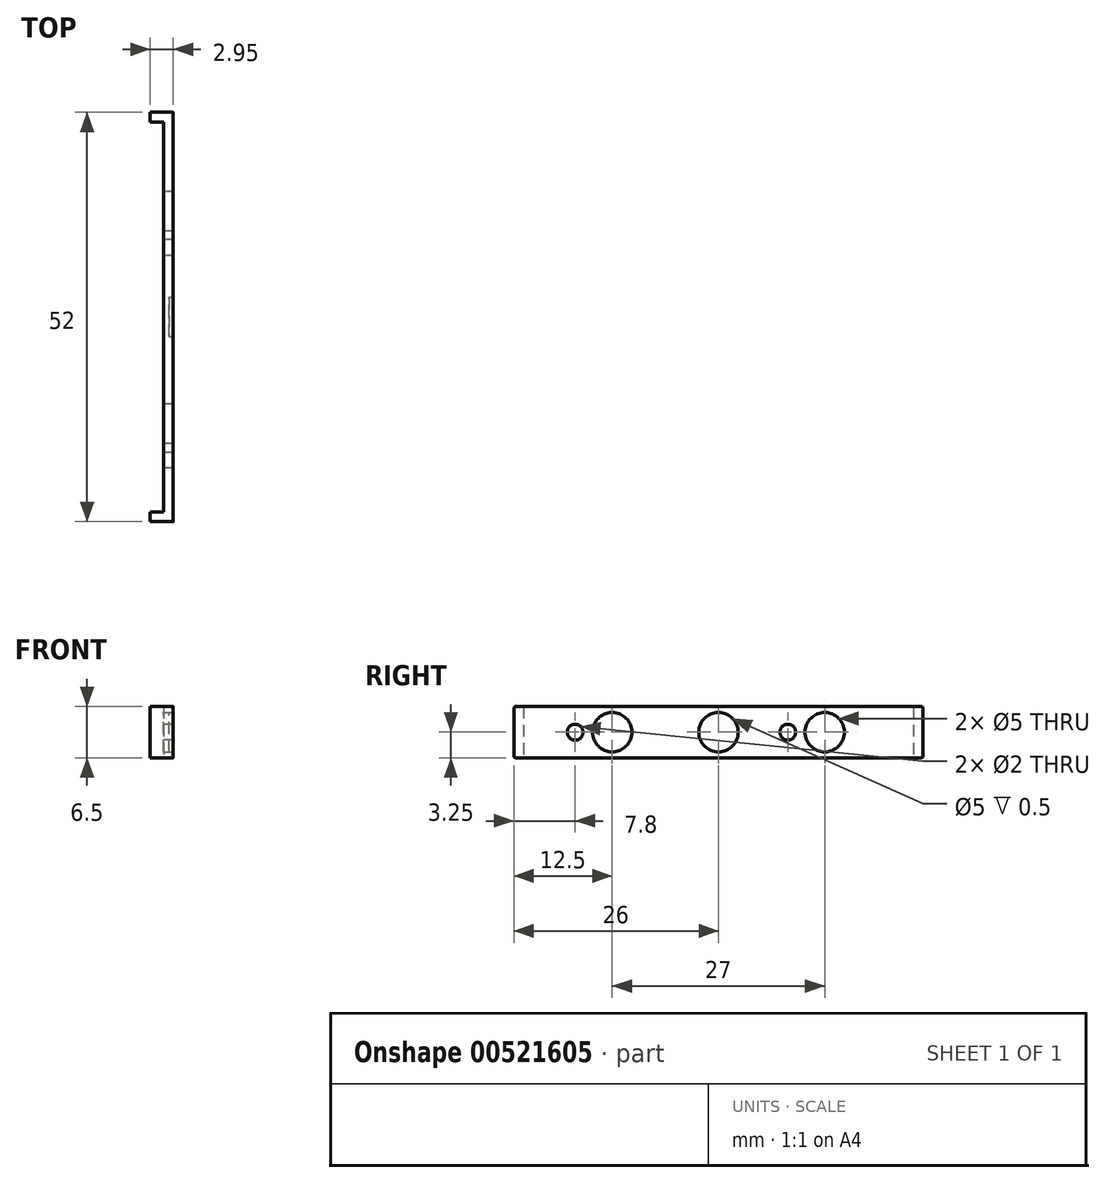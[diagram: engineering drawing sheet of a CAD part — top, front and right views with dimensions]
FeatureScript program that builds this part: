
annotation { "Feature Type Name" : "Feature", "Feature Type Description" : "" }
export const myFeature = defineFeature(function(context is Context, id is Id, definition is map)
    precondition{}
    {
        {
            var Q0;
            Q0=qCreatedBy(makeId("Right.planeOp"),FACE);
            var sketch = newSketch(context, id + "F0", { "sketchPlane" : qUnion([Q0])});
            skLineSegment(sketch, "E0.bottom", {"start": v(26, 3.25) * mm, "end": v(-26, 3.25) * mm});
            skLineSegment(sketch, "E0.top", {"start": v(26, -3.25) * mm, "end": v(-26, -3.25) * mm});
            skLineSegment(sketch, "E0.left", {"start": v(26, 3.25) * mm, "end": v(26, -3.25) * mm});
            skLineSegment(sketch, "E0.right", {"start": v(-26, 3.25) * mm, "end": v(-26, -3.25) * mm});
            skPoint(sketch, "E0.middle", {"position": v(0, 0) * mm});
            skSolve(sketch);
        }
        {
            var Q0;
            Q0=makeQuery(id+"F0.imprint","IMPRINT",FACE,{"disambiguationData":[TD([[makeQuery(id+"F0.imprint","IMPRINT",EDGE,{"derivedFrom":sQuery(id+"F0.wireOp",EDGE,"E0.bottom")}),1.0]])]});
            extrude(context, id + "F1", {"entities" : qUnion([Q0]), "endBound" : BoundingType.SYMMETRIC, "depth" : 1.25 * mm, "offsetDistance" : 25 * mm});
        }
        {
            var Q0;
            Q0=makeQuery(id+"F1.opExtrude","CAP_FACE",FACE,{"disambiguationData":[OSD([sQuery(id+"F0.wireOp",EDGE,"E0.bottom"),sQuery(id+"F0.wireOp",EDGE,"E0.top"),sQuery(id+"F0.wireOp",EDGE,"E0.left"),sQuery(id+"F0.wireOp",EDGE,"E0.right")])],"isStart":true});
            var sketch = newSketch(context, id + "F2", { "sketchPlane" : qUnion([Q0])});
            skLineSegment(sketch, "E1.bottom", {"start": v(-26, 3.25) * mm, "end": v(-24.75, 3.25) * mm});
            skLineSegment(sketch, "E1.top", {"start": v(-26, -3.25) * mm, "end": v(-24.75, -3.25) * mm});
            skLineSegment(sketch, "E1.left", {"start": v(-26, 3.25) * mm, "end": v(-26, -3.25) * mm});
            skLineSegment(sketch, "E1.right", {"start": v(-24.75, 3.25) * mm, "end": v(-24.75, -3.25) * mm});
            skLineSegment(sketch, "E2.bottom", {"start": v(24.75, 3.25) * mm, "end": v(26, 3.25) * mm});
            skLineSegment(sketch, "E2.top", {"start": v(24.75, -3.25) * mm, "end": v(26, -3.25) * mm});
            skLineSegment(sketch, "E2.left", {"start": v(24.75, 3.25) * mm, "end": v(24.75, -3.25) * mm});
            skLineSegment(sketch, "E2.right", {"start": v(26, 3.25) * mm, "end": v(26, -3.25) * mm});
            skSolve(sketch);
        }
        {
            var Q0;
            Q0 = qSketchRegion(id + "F2", true);
            extrude(context, id + "F3", {"entities" : qUnion([Q0]), "operationType" : NewBodyOperationType.ADD, "depth" : 1.7 * mm, "offsetDistance" : 25 * mm});
        }
        {
            var Q0;
            Q0=makeQuery(id+"F3.boolean.opBoolean","MERGE",EDGE,{"derivedFrom":[makeQuery(id+"F1.opExtrude","SWEPT_EDGE",EDGE,{"disambiguationData":[OSD([sQuery(id+"F0.wireOp",EDGE,"E0.bottom"),sQuery(id+"F0.wireOp",EDGE,"E0.right")])]}),makeQuery(id+"F3.opExtrude","SWEPT_EDGE",EDGE,{"disambiguationData":[OSD([sQuery(id+"F2.wireOp",EDGE,"E2.bottom"),sQuery(id+"F2.wireOp",EDGE,"E2.right")])]})]});
            var Q1;
            Q1=makeQuery(id+"F3.boolean.opBoolean","MERGE",EDGE,{"derivedFrom":[makeQuery(id+"F1.opExtrude","SWEPT_EDGE",EDGE,{"disambiguationData":[OSD([sQuery(id+"F0.wireOp",EDGE,"E0.top"),sQuery(id+"F0.wireOp",EDGE,"E0.right")])]}),makeQuery(id+"F3.opExtrude","SWEPT_EDGE",EDGE,{"disambiguationData":[OSD([sQuery(id+"F2.wireOp",EDGE,"E2.top"),sQuery(id+"F2.wireOp",EDGE,"E2.right")])]})]});
            var Q2;
            Q2=makeQuery(id+"F3.boolean.opBoolean","MERGE",EDGE,{"derivedFrom":[makeQuery(id+"F1.opExtrude","SWEPT_EDGE",EDGE,{"disambiguationData":[OSD([sQuery(id+"F0.wireOp",EDGE,"E0.bottom"),sQuery(id+"F0.wireOp",EDGE,"E0.left")])]}),makeQuery(id+"F3.opExtrude","SWEPT_EDGE",EDGE,{"disambiguationData":[OSD([sQuery(id+"F2.wireOp",EDGE,"E1.bottom"),sQuery(id+"F2.wireOp",EDGE,"E1.left")])]})]});
            var Q3;
            Q3=makeQuery(id+"F3.boolean.opBoolean","MERGE",EDGE,{"derivedFrom":[makeQuery(id+"F1.opExtrude","SWEPT_EDGE",EDGE,{"disambiguationData":[OSD([sQuery(id+"F0.wireOp",EDGE,"E0.top"),sQuery(id+"F0.wireOp",EDGE,"E0.left")])]}),makeQuery(id+"F3.opExtrude","SWEPT_EDGE",EDGE,{"disambiguationData":[OSD([sQuery(id+"F2.wireOp",EDGE,"E1.top"),sQuery(id+"F2.wireOp",EDGE,"E1.left")])]})]});
            fillet(context, id + "F4", {"entities" : qUnion([Q0, Q1, Q2, Q3]), "radius" : .25 * mm, "tangentPropagation" : true, "allowEdgeOverflow" : false});
        }
        {
            var Q0;
            Q0=makeQuery(id+"F1.opExtrude","CAP_FACE",FACE,{"disambiguationData":[OSD([sQuery(id+"F0.wireOp",EDGE,"E0.bottom"),sQuery(id+"F0.wireOp",EDGE,"E0.top"),sQuery(id+"F0.wireOp",EDGE,"E0.left"),sQuery(id+"F0.wireOp",EDGE,"E0.right")])],"isStart":false});
            var sketch = newSketch(context, id + "F5", { "sketchPlane" : qUnion([Q0])});
            skCircle(sketch, "E3", {"center": v(-13.5, 0) * mm, "radius": 2.5 * mm});
            skCircle(sketch, "E4", {"center": v(13.5, 0) * mm, "radius": 2.5 * mm});
            skSolve(sketch);
        }
        {
            var Q0;
            Q0 = qSketchRegion(id + "F5", true);
            extrude(context, id + "F6", {"entities" : qUnion([Q0]), "operationType" : NewBodyOperationType.REMOVE, "endBound" : BoundingType.UP_TO_NEXT, "oppositeDirection" : true, "depth" : 25 * mm, "offsetDistance" : 25 * mm});
        }
        {
            var Q0;
            Q0=makeQuery(id+"F1.opExtrude","CAP_FACE",FACE,{"disambiguationData":[OSD([sQuery(id+"F0.wireOp",EDGE,"E0.bottom"),sQuery(id+"F0.wireOp",EDGE,"E0.top"),sQuery(id+"F0.wireOp",EDGE,"E0.left"),sQuery(id+"F0.wireOp",EDGE,"E0.right")])],"isStart":true});
            var sketch = newSketch(context, id + "F7", { "sketchPlane" : qUnion([Q0])});
            skCircle(sketch, "E5", {"center": v(-8.8, 0) * mm, "radius": 1 * mm});
            skCircle(sketch, "E6", {"center": v(18.2, 0) * mm, "radius": 1 * mm});
            skSolve(sketch);
        }
        {
            var Q0;
            Q0 = qSketchRegion(id + "F7", true);
            extrude(context, id + "F8", {"entities" : qUnion([Q0]), "operationType" : NewBodyOperationType.REMOVE, "endBound" : BoundingType.UP_TO_NEXT, "oppositeDirection" : true, "depth" : 1.5 * mm, "offsetDistance" : 25 * mm});
        }
        {
            var Q0;
            Q0=makeQuery(id+"F1.opExtrude","CAP_FACE",FACE,{"disambiguationData":[OSD([sQuery(id+"F0.wireOp",EDGE,"E0.bottom"),sQuery(id+"F0.wireOp",EDGE,"E0.top"),sQuery(id+"F0.wireOp",EDGE,"E0.left"),sQuery(id+"F0.wireOp",EDGE,"E0.right")])],"isStart":false});
            var sketch = newSketch(context, id + "F9", { "sketchPlane" : qUnion([Q0])});
            skCircle(sketch, "E7", {"center": v(0, 0) * mm, "radius": 2.5 * mm});
            skSolve(sketch);
        }
        {
            var Q0;
            Q0 = qSketchRegion(id + "F9", true);
            extrude(context, id + "F10", {"entities" : qUnion([Q0]), "operationType" : NewBodyOperationType.REMOVE, "oppositeDirection" : true, "depth" : .5 * mm, "offsetDistance" : 25 * mm});
        }
    });
